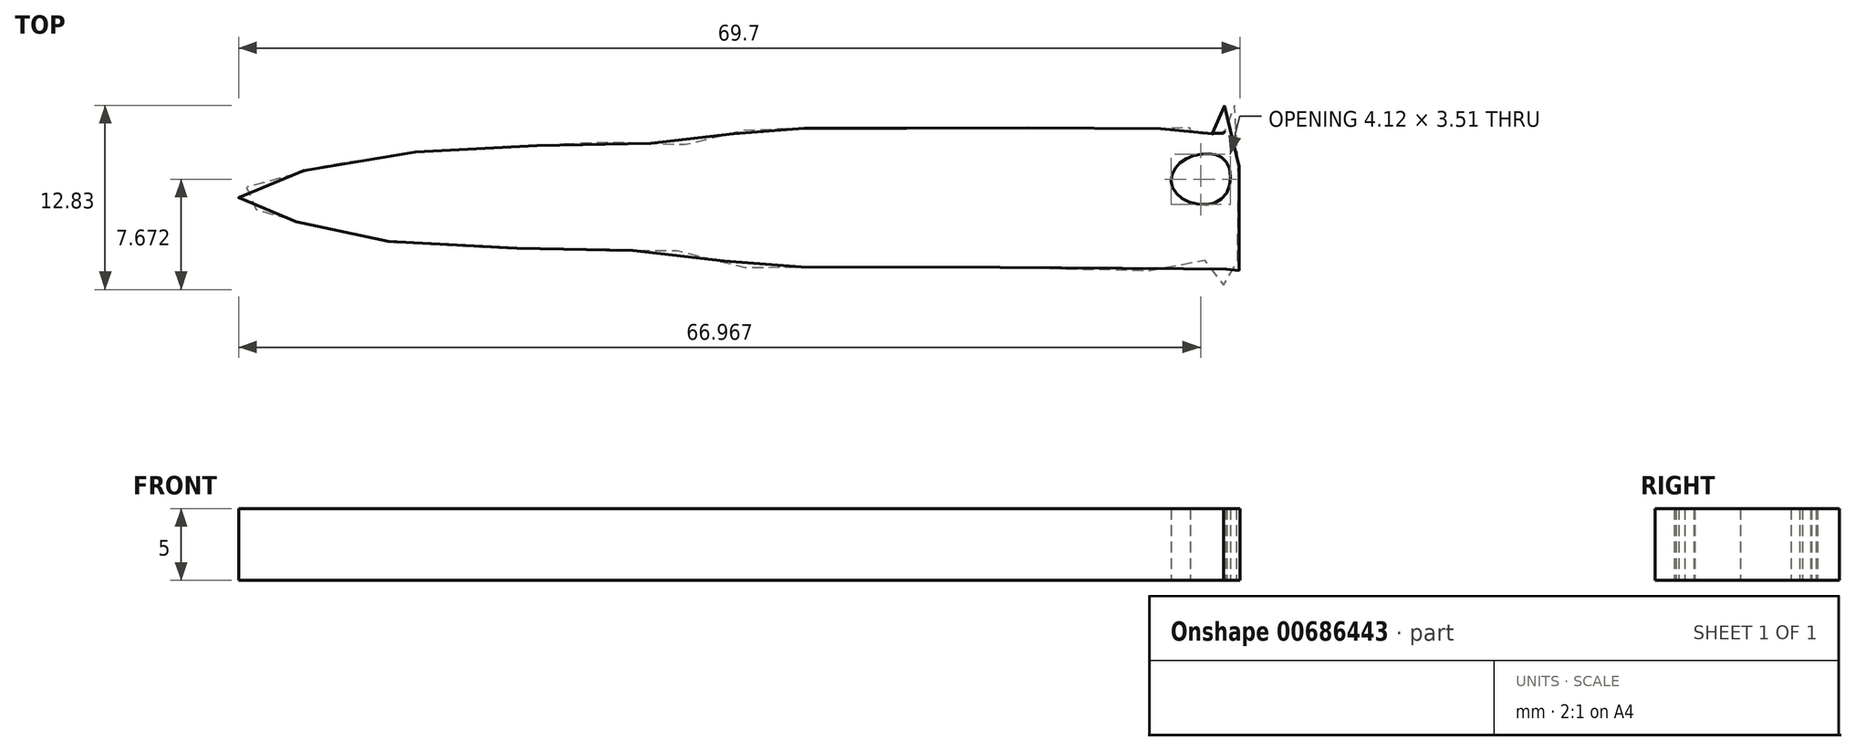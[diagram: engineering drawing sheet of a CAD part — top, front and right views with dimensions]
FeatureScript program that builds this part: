
annotation { "Feature Type Name" : "Feature", "Feature Type Description" : "" }
export const myFeature = defineFeature(function(context is Context, id is Id, definition is map)
    precondition{}
    {
        {
            var Q0;
            Q0=qCreatedBy(makeId("Top.planeOp"),FACE);
            var sketch = newSketch(context, id + "F0", { "sketchPlane" : qUnion([Q0])});
            skFitSpline(sketch, "E0", {"points": [v(-32.96, 16.15) * mm, v(-36.53, 16.1) * mm, v(-37.68, 15.82) * mm, v(-40.68, 15.04) * mm, v(-44.7, 15.16) * mm, v(-51.48, 14.96) * mm, v(-59.04, 14.59) * mm, v(-64.8, 13.8) * mm, v(-70.98, 12.37) * mm, v(-72.2, 11.7) * mm, v(-72.3, 11.2) * mm, v(-71.32, 10.57) * mm, v(-68.88, 9.79) * mm, v(-64.14, 8.71) * mm, v(-60.18, 8.08) * mm, v(-50.41, 7.73) * mm, v(-44.8, 7.64) * mm, v(-40.55, 7.49) * mm, v(-37.13, 6.46) * mm, v(-35.57, 6.41) * mm, v(-20.81, 6.51) * mm, v(-6.11, 6.51) * mm, v(-5.96, 6.76) * mm, v(-3.72, 6.85) * mm, v(-3.62, 6.17) * mm, v(-3.67, 5.05) * mm, v(-2.79, 5.1) * mm, v(-2.79, 6.85) * mm, v(-2.74, 11.93) * mm, v(-2.84, 17.7) * mm, v(-3, 17.75) * mm, v(-3.72, 17.7) * mm, v(-3.74, 17.34) * mm, v(-3.73, 15.87) * mm, v(-3.94, 15.8) * mm, v(-4.36, 15.8) * mm, v(-6.04, 15.88) * mm, v(-6.07, 16.16) * mm, v(-6.54, 16.18) * mm, v(-14.76, 16.16) * mm, v(-20.57, 16.16) * mm, v(-29.1, 16.16) * mm, v(-32.96, 16.15) * mm]});
            skFitSpline(sketch, "E1", {"points": [v(-6.8, 13.74) * mm, v(-7.39, 12.23) * mm, v(-5.96, 10.96) * mm, v(-3.73, 11.4) * mm, v(-3.48, 13.64) * mm, v(-4.8, 14.38) * mm, v(-6.8, 13.74) * mm]});
            skSolve(sketch);
        }
        {
            var Q0;
            Q0 = qSketchRegion(id + "F0", true);
            extrude(context, id + "F1", {"entities" : qUnion([Q0]), "depth" : 5 * mm, "offsetDistance" : 25.4 * mm});
        }
    });
